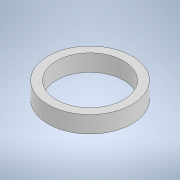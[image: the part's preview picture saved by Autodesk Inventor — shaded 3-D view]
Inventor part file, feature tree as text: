
AUTODESK INVENTOR PART (.ipt)
format: ipt  version: 2020.3 (Build 243373000, 373)  size: 98,816 bytes
history: native  units: mm
features: extrude x1, sketch x1
ambient origin geometry x8: Origin, YZ Plane, XZ Plane, XY Plane, X Axis, Y Axis, Z Axis, Center Point
bodies: Solid1 (feature_tree)
feature tree (2):
  extrude  "Extrusion1"  Depth=10.0mm
  sketch  "Sketch1"  dims[d0=40.0mm d1=50.0mm d2=10.0mm d3=0.0mm]
